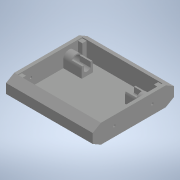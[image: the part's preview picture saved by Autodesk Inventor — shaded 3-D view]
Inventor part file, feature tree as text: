
AUTODESK INVENTOR PART (.ipt)
format: ipt  version: 2020 (Build 240168000, 168)  size: 242,176 bytes
history: native  units: in
note: dims shown in document units (in); Inventor stores cm internally (conversion verified against a paired STEP export)
features: extrude x7, sketch x7, projected_geometry x4, mirror x2
ambient origin geometry x8: Origin, YZ Plane, XZ Plane, XY Plane, X Axis, Y Axis, Z Axis, Center Point
bodies: Solid1 (feature_tree)
feature tree (20):
  extrude  "Extrusion1"  Depth=5.9055in
  extrude  "Extrusion2"  TaperAngle=0.0deg  [1 undecoded]
  extrude  "Extrusion3"  Depth=1.2598in
  extrude  "Extrusion4"  Depth=0.315in
  extrude  "Extrusion5"  TaperAngle=0.0deg  [1 undecoded]
  extrude  "Extrusion6"  Depth=0.689in
  mirror  "Mirror1"
  extrude  "Extrusion7"  Depth=0.0787in
  mirror  "Mirror2"
  sketch  "Sketch1"  dims[d0=1.378in d1=5.9055in]
  sketch  "Sketch2"  dims[d2=6.2992in d3=0.0in]
  projected_geometry  "Projected Loop1"
  sketch  "Sketch3"  dims[d4=0.2362in d5=1.2598in]
  projected_geometry  "Projected Loop2"
  projected_geometry  "Projected Loop3"
  sketch  "Sketch4"  dims[d6=0.0in d8=0.315in]
  sketch  "Sketch5"  dims[d10=1.1898in d11=0.0in]
  projected_geometry  "Projected Loop4"
  sketch  "Sketch6"  dims[d12=0.6496in d13=0.689in]
  sketch  "Sketch7"  dims[d14=1.5748in d15=0.0787in d16=0.5512in d17=0.0in d18=0.6102in d19=0.4803in d20=0.7874in d21=0.0in d22=0.1654in d23=6.063in d24=0.0in d25=0.5967in d26=0.1575in d27=1.5748in d28=0.0in d29=0.0in]
note: 2 required parameter values undecoded (feature->parameter linkage not recoverable at this tier; creation-order binding heuristic only, values carry confidence <= 0.55)
